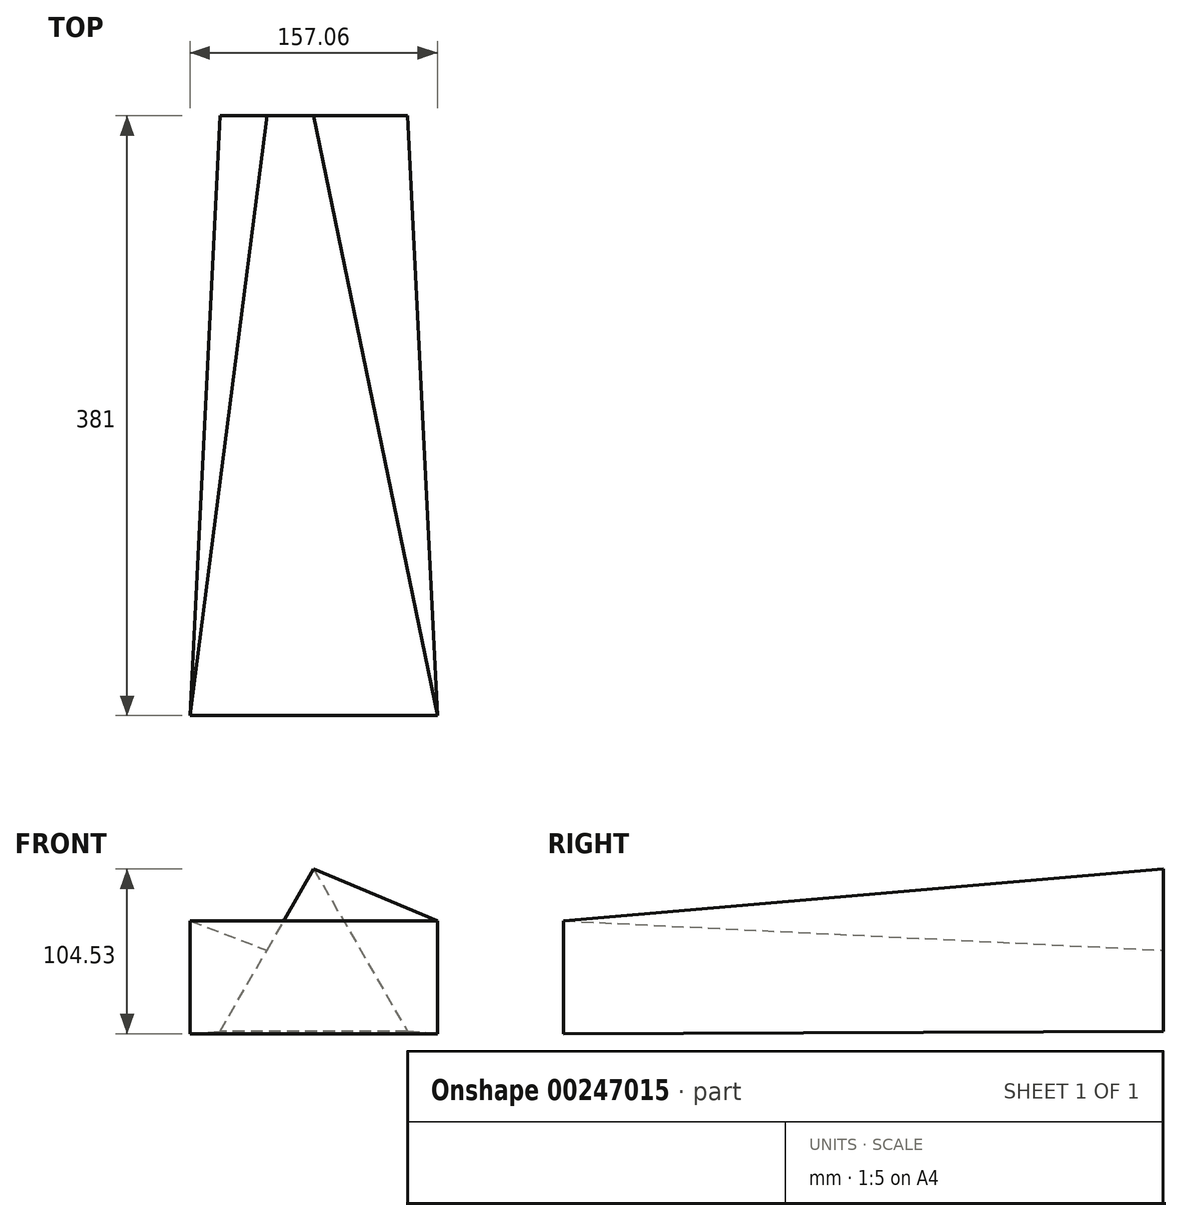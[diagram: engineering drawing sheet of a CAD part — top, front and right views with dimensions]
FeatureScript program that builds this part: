
annotation { "Feature Type Name" : "Feature", "Feature Type Description" : "" }
export const myFeature = defineFeature(function(context is Context, id is Id, definition is map)
    precondition{}
    {
        {
            var Q0;
            Q0=qCreatedBy(makeId("Front.planeOp"),FACE);
            var sketch = newSketch(context, id + "F0", { "sketchPlane" : qUnion([Q0])});
            skLineSegment(sketch, "E0.bottom", {"start": v(78.53, -35.83) * mm, "end": v(-78.53, -35.83) * mm});
            skLineSegment(sketch, "E0.top", {"start": v(78.53, 35.83) * mm, "end": v(-78.53, 35.83) * mm});
            skLineSegment(sketch, "E0.left", {"start": v(78.53, -35.83) * mm, "end": v(78.53, 35.83) * mm});
            skLineSegment(sketch, "E0.right", {"start": v(-78.53, -35.83) * mm, "end": v(-78.53, 35.83) * mm});
            skPoint(sketch, "E0.middle", {"position": v(0, 0) * mm});
            skSolve(sketch);
        }
        {
            var Q0;
            Q0=qCreatedBy(makeId("Front.planeOp"),FACE);
            cPlane(context, id + "F1", {"entities" : qUnion([Q0]), "cplaneType" : CPlaneType.OFFSET, "offset" : 381 * mm, "oppositeDirection" : true, "width" : 152.4 * mm, "height" : 152.4 * mm});
        }
        {
            var Q0;
            Q0=qCreatedBy(id+"F1.planeOp",FACE);
            var sketch = newSketch(context, id + "F2", { "sketchPlane" : qUnion([Q0])});
            skCircle(sketch, "E1.cCircle", {"center": v(0, 0) * mm, "radius": 34.35 * mm, "construction": true});
            skLineSegment(sketch, "E1.0", {"start": v(59.5, -34.35) * mm, "end": v(-59.5, -34.35) * mm});
            skLineSegment(sketch, "E1.1", {"start": v(-59.5, -34.35) * mm, "end": v(0, 68.7) * mm});
            skLineSegment(sketch, "E1.2", {"start": v(0, 68.7) * mm, "end": v(59.5, -34.35) * mm});
            skPoint(sketch, "E1.0.midPoint", {"position": v(0, -34.35) * mm});
            skSolve(sketch);
        }
        {
            var Q0;
            Q0=makeQuery(id+"F0.imprint","IMPRINT",FACE,{"disambiguationData":[TD([[makeQuery(id+"F0.imprint","IMPRINT",EDGE,{"derivedFrom":sQuery(id+"F0.wireOp",EDGE,"E0.bottom")}),-1.0]])]});
            var Q1;
            Q1=makeQuery(id+"F2.imprint","IMPRINT",FACE,{"disambiguationData":[TD([[makeQuery(id+"F2.imprint","IMPRINT",EDGE,{"derivedFrom":sQuery(id+"F2.wireOp",EDGE,"E1.0")}),-1.0]])]});
            loft(context, id + "F3", {"sheetProfilesArray" : [{ "sheetProfileEntities" : qUnion([Q0]) }, { "sheetProfileEntities" : qUnion([Q1]) }]});
        }
    });
